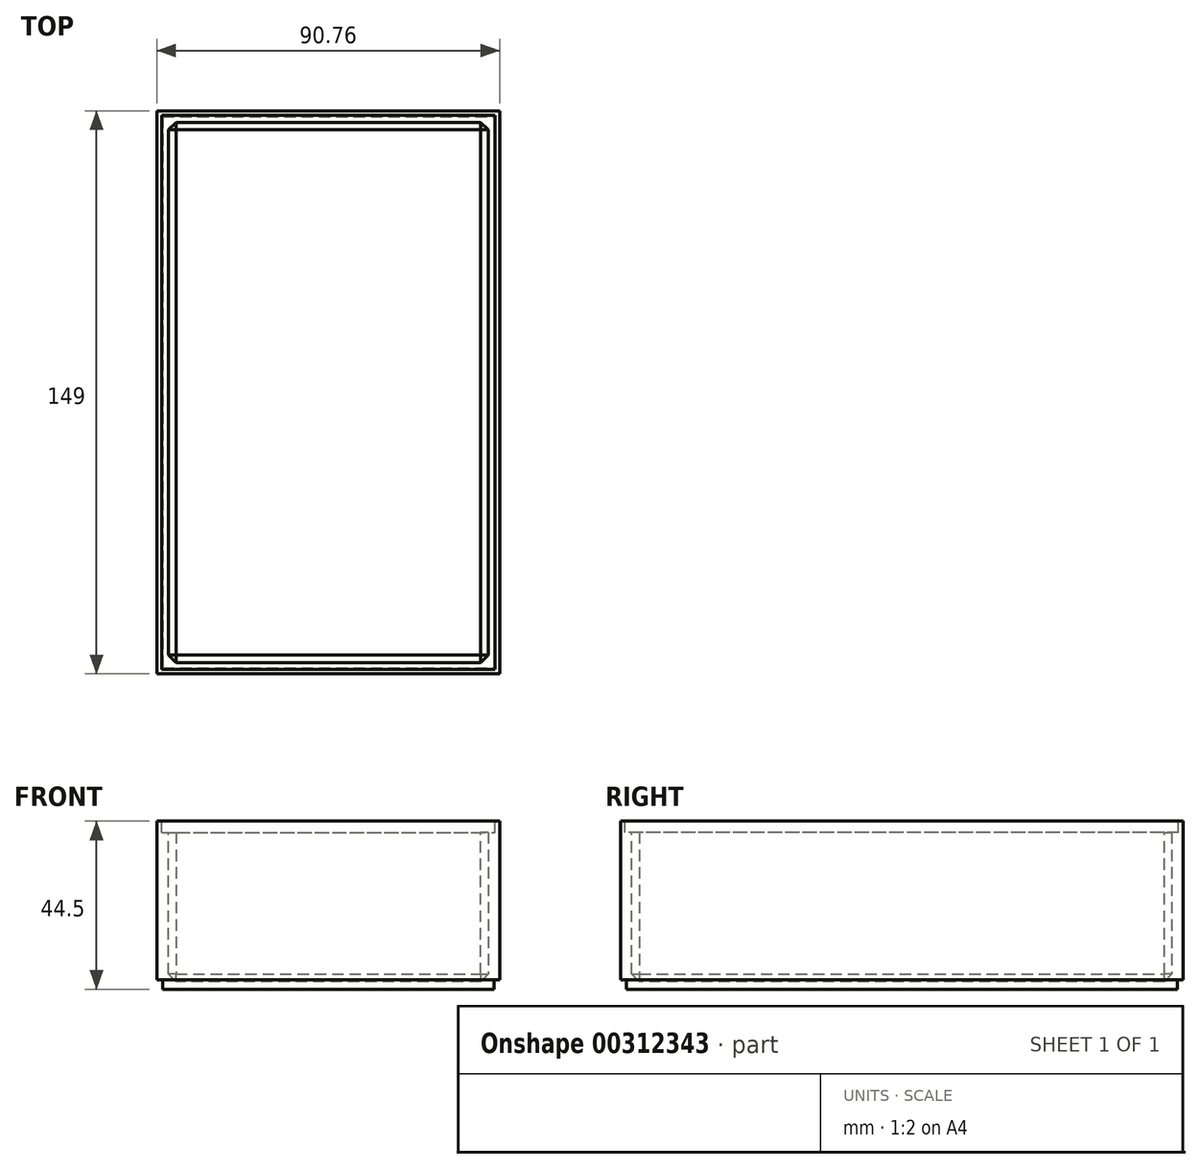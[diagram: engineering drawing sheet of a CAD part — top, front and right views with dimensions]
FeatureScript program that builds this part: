
annotation { "Feature Type Name" : "Feature", "Feature Type Description" : "" }
export const myFeature = defineFeature(function(context is Context, id is Id, definition is map)
    precondition{}
    {
        {
            assignVariable(context, id + "F0", {"name" : "BoxHeight", "anyValue" : 44.5 * mm});
        }
        {
            var Q0;
            Q0=qCreatedBy(makeId("Top.planeOp"),FACE);
            var sketch = newSketch(context, id + "F1", { "sketchPlane" : qUnion([Q0])});
            skLineSegment(sketch, "E0.bottom", {"start": v(-45.37, 74.5) * mm, "end": v(45.38, 74.5) * mm});
            skLineSegment(sketch, "E0.top", {"start": v(-45.38, -74.5) * mm, "end": v(45.37, -74.5) * mm});
            skLineSegment(sketch, "E0.left", {"start": v(-45.37, 74.5) * mm, "end": v(-45.38, -74.5) * mm});
            skLineSegment(sketch, "E0.right", {"start": v(45.38, 74.5) * mm, "end": v(45.37, -74.5) * mm});
            skPoint(sketch, "E0.middle", {"position": v(0, 0) * mm});
            skLineSegment(sketch, "E1.0", {"start": v(-42.37, 71.5) * mm, "end": v(42.38, 71.5) * mm});
            skLineSegment(sketch, "E1.1", {"start": v(-42.37, 71.5) * mm, "end": v(-42.38, -71.5) * mm});
            skLineSegment(sketch, "E1.2", {"start": v(-42.38, -71.5) * mm, "end": v(42.37, -71.5) * mm});
            skLineSegment(sketch, "E1.3", {"start": v(42.38, 71.5) * mm, "end": v(42.37, -71.5) * mm});
            skSolve(sketch);
        }
        {
            var Q0;
            Q0=makeQuery(id+"F1.imprint","IMPRINT",FACE,{"disambiguationData":[TD([[makeQuery(id+"F1.imprint","IMPRINT",EDGE,{"derivedFrom":sQuery(id+"F1.wireOp",EDGE,"E0.bottom")}),-1.0]])]});
            extrude(context, id + "F2", {"entities" : qUnion([Q0]), "depth" : getVariable(context, 'BoxHeight')});
        }
        {
            var Q0;
            Q0=qSketchRegion(id+"F1",true);
            var Q1;
            Q1=makeQuery(id+"F1.imprint","IMPRINT",FACE,{"disambiguationData":[TD([[makeQuery(id+"F1.imprint","IMPRINT",EDGE,{"derivedFrom":sQuery(id+"F1.wireOp",EDGE,"E1.0")}),-1.0]])]});
            extrude(context, id + "F3", {"entities" : qUnion([Q0, Q1]), "operationType" : NewBodyOperationType.ADD, "depth" : 2 * mm});
        }
        {
            var Q0;
            Q0=makeQuery(id+"F3.boolean.opBoolean","INTERSECT",EDGE,{"derivedFrom":[makeQuery(id+"F2.opExtrude","SWEPT_FACE",FACE,{"disambiguationData":[OSD([sQuery(id+"F1.wireOp",EDGE,"E1.0")])]}),makeQuery(id+"F3.opExtrude","CAP_FACE",FACE,{"disambiguationData":[OSD([sQuery(id+"F1.wireOp",EDGE,"E0.bottom"),sQuery(id+"F1.wireOp",EDGE,"E0.top"),sQuery(id+"F1.wireOp",EDGE,"E0.left"),sQuery(id+"F1.wireOp",EDGE,"E0.right")])],"isStart":false})]});
            var Q1;
            Q1=makeQuery(id+"F3.boolean.opBoolean","INTERSECT",EDGE,{"derivedFrom":[makeQuery(id+"F2.opExtrude","SWEPT_FACE",FACE,{"disambiguationData":[OSD([sQuery(id+"F1.wireOp",EDGE,"E1.3")])]}),makeQuery(id+"F3.opExtrude","CAP_FACE",FACE,{"disambiguationData":[OSD([sQuery(id+"F1.wireOp",EDGE,"E0.bottom"),sQuery(id+"F1.wireOp",EDGE,"E0.top"),sQuery(id+"F1.wireOp",EDGE,"E0.left"),sQuery(id+"F1.wireOp",EDGE,"E0.right")])],"isStart":false})]});
            var Q2;
            Q2=makeQuery(id+"F3.boolean.opBoolean","INTERSECT",EDGE,{"derivedFrom":[makeQuery(id+"F2.opExtrude","SWEPT_FACE",FACE,{"disambiguationData":[OSD([sQuery(id+"F1.wireOp",EDGE,"E1.1")])]}),makeQuery(id+"F3.opExtrude","CAP_FACE",FACE,{"disambiguationData":[OSD([sQuery(id+"F1.wireOp",EDGE,"E0.bottom"),sQuery(id+"F1.wireOp",EDGE,"E0.top"),sQuery(id+"F1.wireOp",EDGE,"E0.left"),sQuery(id+"F1.wireOp",EDGE,"E0.right")])],"isStart":false})]});
            var Q3;
            Q3=makeQuery(id+"F3.boolean.opBoolean","INTERSECT",EDGE,{"derivedFrom":[makeQuery(id+"F2.opExtrude","SWEPT_FACE",FACE,{"disambiguationData":[OSD([sQuery(id+"F1.wireOp",EDGE,"E1.2")])]}),makeQuery(id+"F3.opExtrude","CAP_FACE",FACE,{"disambiguationData":[OSD([sQuery(id+"F1.wireOp",EDGE,"E0.bottom"),sQuery(id+"F1.wireOp",EDGE,"E0.top"),sQuery(id+"F1.wireOp",EDGE,"E0.left"),sQuery(id+"F1.wireOp",EDGE,"E0.right")])],"isStart":false})]});
            var Q4;
            Q4=makeQuery(id+"F2.opExtrude","SWEPT_EDGE",EDGE,{"disambiguationData":[OSD([sQuery(id+"F1.wireOp",EDGE,"E1.2"),sQuery(id+"F1.wireOp",EDGE,"E1.3")])]});
            var Q5;
            Q5=makeQuery(id+"F2.opExtrude","SWEPT_EDGE",EDGE,{"disambiguationData":[OSD([sQuery(id+"F1.wireOp",EDGE,"E1.0"),sQuery(id+"F1.wireOp",EDGE,"E1.3")])]});
            var Q6;
            Q6=makeQuery(id+"F2.opExtrude","SWEPT_EDGE",EDGE,{"disambiguationData":[OSD([sQuery(id+"F1.wireOp",EDGE,"E1.0"),sQuery(id+"F1.wireOp",EDGE,"E1.1")])]});
            var Q7;
            Q7=makeQuery(id+"F2.opExtrude","SWEPT_EDGE",EDGE,{"disambiguationData":[OSD([sQuery(id+"F1.wireOp",EDGE,"E1.1"),sQuery(id+"F1.wireOp",EDGE,"E1.2")])]});
            chamfer(context, id + "F4", {"entities" : qUnion([Q0, Q1, Q2, Q3, Q4, Q5, Q6, Q7]), "width" : 2 * mm, "tangentPropagation" : true});
        }
        {
            var Q0;
            Q0=makeQuery(id+"F2.opExtrude","CAP_FACE",FACE,{"disambiguationData":[OSD([sQuery(id+"F1.wireOp",EDGE,"E0.bottom"),sQuery(id+"F1.wireOp",EDGE,"E0.top"),sQuery(id+"F1.wireOp",EDGE,"E0.left"),sQuery(id+"F1.wireOp",EDGE,"E0.right"),sQuery(id+"F1.wireOp",EDGE,"E1.0"),sQuery(id+"F1.wireOp",EDGE,"E1.1"),sQuery(id+"F1.wireOp",EDGE,"E1.2"),sQuery(id+"F1.wireOp",EDGE,"E1.3")])],"isStart":false});
            var sketch = newSketch(context, id + "F5", { "sketchPlane" : qUnion([Q0])});
            skLineSegment(sketch, "E2.0", {"start": v(-45.37, 74.5) * mm, "end": v(45.38, 74.5) * mm});
            skLineSegment(sketch, "E2.1", {"start": v(45.38, 74.5) * mm, "end": v(45.37, -74.5) * mm});
            skLineSegment(sketch, "E2.2", {"start": v(-45.37, 74.5) * mm, "end": v(-45.38, -74.5) * mm});
            skLineSegment(sketch, "E2.3", {"start": v(-45.38, -74.5) * mm, "end": v(45.37, -74.5) * mm});
            skLineSegment(sketch, "E3.0", {"start": v(-44.17, 73.3) * mm, "end": v(-44.18, -73.3) * mm});
            skLineSegment(sketch, "E3.1", {"start": v(-44.17, 73.3) * mm, "end": v(44.17, 73.3) * mm});
            skLineSegment(sketch, "E3.2", {"start": v(44.18, 73.3) * mm, "end": v(44.17, -73.3) * mm});
            skLineSegment(sketch, "E3.3", {"start": v(-44.18, -73.3) * mm, "end": v(44.17, -73.3) * mm});
            skSolve(sketch);
        }
        {
            var Q0;
            Q0=makeQuery(id+"F5.imprint","IMPRINT",FACE,{"disambiguationData":[TD([[makeQuery(id+"F5.imprint","IMPRINT",EDGE,{"derivedFrom":sQuery(id+"F5.wireOp",EDGE,"E3.0")}),1.0]])]});
            extrude(context, id + "F6", {"entities" : qUnion([Q0]), "operationType" : NewBodyOperationType.REMOVE, "oppositeDirection" : true, "depth" : 3 * mm});
        }
        {
            var Q0;
            {var subQ0=sQuery(id+"F1.wireOp",EDGE,"E0.right");var subQ1=sQuery(id+"F1.wireOp",EDGE,"E0.left");var subQ2=sQuery(id+"F1.wireOp",EDGE,"E0.top");var subQ3=sQuery(id+"F1.wireOp",EDGE,"E0.bottom");Q0=makeQuery(id+"F3.boolean.opBoolean","MERGE",FACE,{"derivedFrom":[makeQuery(id+"F2.opExtrude","CAP_FACE",FACE,{"disambiguationData":[OSD([subQ3,subQ2,subQ1,subQ0,sQuery(id+"F1.wireOp",EDGE,"E1.0"),sQuery(id+"F1.wireOp",EDGE,"E1.1"),sQuery(id+"F1.wireOp",EDGE,"E1.2"),sQuery(id+"F1.wireOp",EDGE,"E1.3")])],"isStart":true}),makeQuery(id+"F3.opExtrude","CAP_FACE",FACE,{"disambiguationData":[OSD([subQ3,subQ2,subQ1,subQ0])],"isStart":true})]});}
            var sketch = newSketch(context, id + "F7", { "sketchPlane" : qUnion([Q0])});
            skLineSegment(sketch, "E4.0", {"start": v(-45.37, -74.5) * mm, "end": v(-45.38, 74.5) * mm});
            skLineSegment(sketch, "E5.0", {"start": v(-45.38, 74.5) * mm, "end": v(45.37, 74.5) * mm});
            skLineSegment(sketch, "E6.0", {"start": v(45.38, -74.5) * mm, "end": v(45.37, 74.5) * mm});
            skLineSegment(sketch, "E7.0", {"start": v(-45.37, -74.5) * mm, "end": v(45.38, -74.5) * mm});
            skLineSegment(sketch, "E8.0", {"start": v(-43.87, -73) * mm, "end": v(-43.88, 73) * mm});
            skLineSegment(sketch, "E8.1", {"start": v(-43.87, -73) * mm, "end": v(43.88, -73) * mm});
            skLineSegment(sketch, "E8.2", {"start": v(43.88, -73) * mm, "end": v(43.87, 73) * mm});
            skLineSegment(sketch, "E8.3", {"start": v(-43.88, 73) * mm, "end": v(43.87, 73) * mm});
            skSolve(sketch);
        }
        {
            var Q0;
            Q0=makeQuery(id+"F7.imprint","IMPRINT",FACE,{"disambiguationData":[TD([[makeQuery(id+"F7.imprint","IMPRINT",EDGE,{"derivedFrom":sQuery(id+"F7.wireOp",EDGE,"E4.0")}),-1.0]])]});
            extrude(context, id + "F8", {"entities" : qUnion([Q0]), "operationType" : NewBodyOperationType.REMOVE, "oppositeDirection" : true, "depth" : 2.5 * mm});
        }
    });
